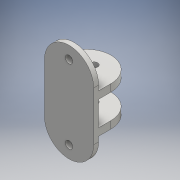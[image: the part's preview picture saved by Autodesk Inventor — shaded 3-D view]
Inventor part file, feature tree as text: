
AUTODESK INVENTOR PART (.ipt)
format: ipt  version: 2016 (Build 200138000, 138)  size: 145,408 bytes
history: native  units: mm
features: sketch x4, extrude x2, fillet x2, hole x2
ambient origin geometry x8: Origin, YZ Plane, XZ Plane, XY Plane, X Axis, Y Axis, Z Axis, Center Point
bodies: Solid1 (feature_tree)
feature tree (10):
  extrude  "Extrusion1"  Depth=20.0mm
  extrude  "Extrusion2"  Depth=3.0mm
  fillet  "Fillet1"  Radius=5.0mm
  hole  "Hole1"  [1 undecoded]
  fillet  "Fillet2"  Radius=5.0mm
  hole  "Hole2"  [1 undecoded]
  sketch  "Sketch1"  dims[d0=20.0mm d1=40.0mm]
  sketch  "Sketch3"  dims[d2=2.0mm d3=0.0mm d6=3.0mm d7=5.0mm]
  sketch  "Sketch4"  dims[d8=15.0mm d9=0.0mm d10=10.0mm d11=5.0mm]
  sketch  "Sketch5"  dims[d12=5.0mm d13=3.0mm d14=6.0mm d15=4.0mm d16=2.0mm d17=90.0deg d18=8.0mm d19=20.594885mm d20=10.0mm d21=3.0mm d22=6.0mm d23=4.0mm d24=2.0mm d25=90.0deg d26=8.0mm d27=20.594885mm]
note: 2 required parameter values undecoded (feature->parameter linkage not recoverable at this tier; creation-order binding heuristic only, values carry confidence <= 0.55)
